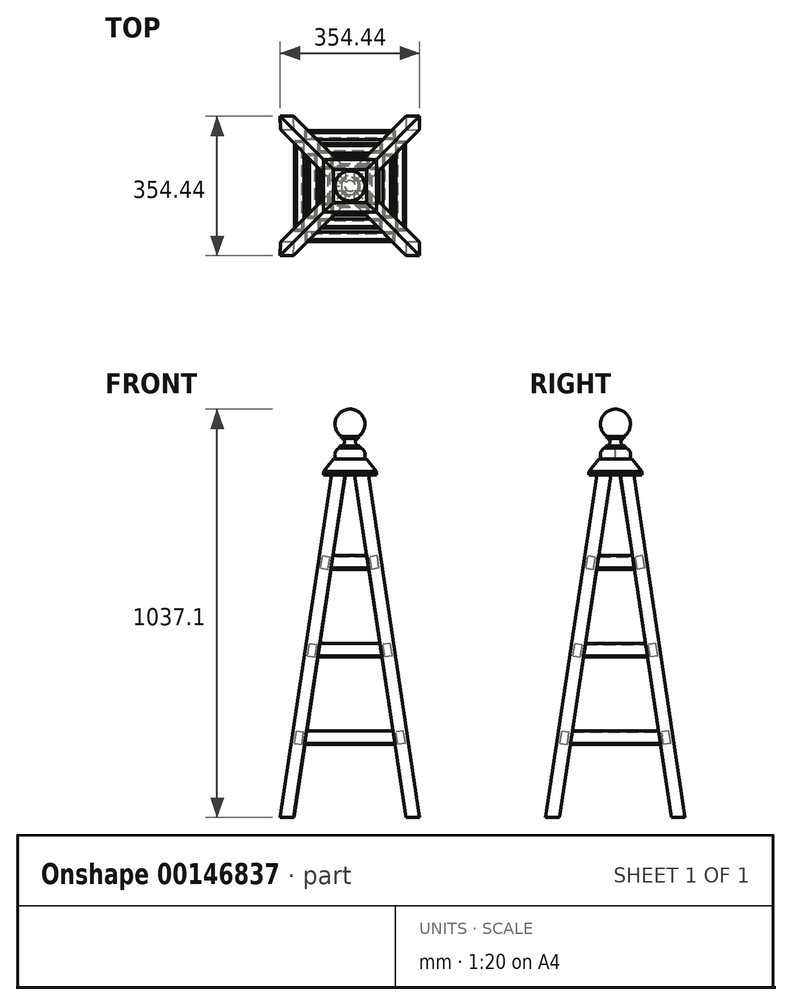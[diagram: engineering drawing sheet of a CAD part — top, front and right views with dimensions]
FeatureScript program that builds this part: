
annotation { "Feature Type Name" : "Feature", "Feature Type Description" : "" }
export const myFeature = defineFeature(function(context is Context, id is Id, definition is map)
    precondition{}
    {
        {
            assignVariable(context, id + "F0", {"name" : "Angle0", "anyValue" : 12 * degree});
        }
        {
            assignVariable(context, id + "F1", {"name" : "CentreSpread0", "anyValue" : 12});
        }
        {
            assignVariable(context, id + "F2", {"name" : "ArmOffset0", "anyValue" : ((((900 - (sqrt(34 * 34 * 2) * sin(getVariable(context, 'Angle0')))) * sin(getVariable(context, 'Angle0')) + (sqrt(17 * 17 * 2) / cos(getVariable(context, 'Angle0')))) * sin(45 * degree)) + getVariable(context, 'CentreSpread0')) * mm});
        }
        {
            var Q0;
            Q0=qCreatedBy(makeId("Front.planeOp"),FACE);
            var sketch = newSketch(context, id + "F3", { "sketchPlane" : qUnion([Q0])});
            skLineSegment(sketch, "E0.bottom", {"start": v(-17, 450) * mm, "end": v(17, 450) * mm});
            skLineSegment(sketch, "E0.top", {"start": v(-17, -450) * mm, "end": v(17, -450) * mm});
            skLineSegment(sketch, "E0.left", {"start": v(-17, 450) * mm, "end": v(-17, -450) * mm});
            skLineSegment(sketch, "E0.right", {"start": v(17, 450) * mm, "end": v(17, -450) * mm});
            skPoint(sketch, "E0.middle", {"position": v(0, 0) * mm});
            skLineSegment(sketch, "E1", {"start": v(0, 0) * mm, "end": v(0, 406.37) * mm, "construction": true});
            skSolve(sketch);
        }
        {
            var Q0;
            Q0=sQuery(id+"F3.wireOp",EDGE,"E1");
            cPlane(context, id + "F4", {"entities" : qUnion([Q0]), "cplaneType" : CPlaneType.LINE_ANGLE, "offset" : 25 * mm, "angle" : 45 * degree, "width" : 150 * mm, "height" : 150 * mm});
        }
        {
            var Q0;
            Q0=sQuery(id+"F3.wireOp",EDGE,"E1");
            cPlane(context, id + "F5", {"entities" : qUnion([Q0]), "cplaneType" : CPlaneType.LINE_ANGLE, "offset" : 25 * mm, "angle" : 135 * degree, "width" : 150 * mm, "height" : 150 * mm});
        }
        {
            var Q0;
            Q0=qCreatedBy(id+"F5.planeOp",FACE);
            cPlane(context, id + "F6", {"entities" : qUnion([Q0]), "cplaneType" : CPlaneType.OFFSET, "offset" : (sqrt(17 * 17 * 2)) * mm, "oppositeDirection" : true, "width" : 150 * mm, "height" : 150 * mm});
        }
        {
            var Q0;
            Q0=qSketchRegion(id+"F3",true);
            extrude(context, id + "F7", {"entities" : qUnion([Q0]), "depth" : 17 * mm, "hasSecondDirection" : true, "secondDirectionOppositeDirection" : true, "secondDirectionDepth" : 17 * mm});
        }
        {
            var Q0;
            Q0=qCreatedBy(id+"F4.planeOp",FACE);
            var sketch = newSketch(context, id + "F8", { "sketchPlane" : qUnion([Q0])});
            skLineSegment(sketch, "E2", {"start": v(24.04, 450) * mm, "end": v(-24.04, 439.78) * mm});
            skLineSegment(sketch, "E3", {"start": v(-24.04, 450) * mm, "end": v(24.04, 450) * mm});
            skLineSegment(sketch, "E4", {"start": v(-24.04, 450) * mm, "end": v(-24.04, 439.78) * mm});
            skLineSegment(sketch, "E5", {"start": v(-24.04, -450) * mm, "end": v(24.04, -439.78) * mm});
            skLineSegment(sketch, "E6", {"start": v(-24.04, -450) * mm, "end": v(24.04, -450) * mm});
            skLineSegment(sketch, "E7", {"start": v(24.04, -450) * mm, "end": v(24.04, -439.78) * mm});
            skSolve(sketch);
        }
        {
            var Q0;
            Q0=qSketchRegion(id+"F8",true);
            extrude(context, id + "F9", {"entities" : qUnion([Q0]), "operationType" : NewBodyOperationType.REMOVE, "depth" : (sqrt(17 * 17 * 2)) * mm, "hasSecondDirection" : true, "secondDirectionOppositeDirection" : true, "secondDirectionDepth" : (sqrt(17 * 17 * 2)) * mm});
        }
        {
            var Q0;
            Q0=qCreatedBy(id+"F6.planeOp",FACE);
            var sketch = newSketch(context, id + "F10", { "sketchPlane" : qUnion([Q0])});
            skLineSegment(sketch, "E8", {"start": v(-24.04, -450) * mm, "end": v(24.04, -450) * mm, "construction": true});
            skSolve(sketch);
        }
        {
            var Q0;
            Q0=makeQuery(id+"F7.opExtrude","SWEPT_BODY",BODY,{"disambiguationData":[OSD([sQuery(id+"F3.wireOp",EDGE,"E0.bottom"),sQuery(id+"F3.wireOp",EDGE,"E0.top"),sQuery(id+"F3.wireOp",EDGE,"E0.left"),sQuery(id+"F3.wireOp",EDGE,"E0.right")])]});
            var Q1;
            Q1=sQuery(id+"F10.wireOp",EDGE,"E8");
            transform(context, id + "F11", {"entities" : qUnion([Q0]), "transformType" : TransformType.ROTATION, "transformAxis" : qUnion([Q1]), "angle" : getVariable(context, 'Angle0'), "makeCopy" : false});
        }
        {
            var Q0;
            Q0=makeQuery(id+"F7.opExtrude","SWEPT_BODY",BODY,{"disambiguationData":[OSD([sQuery(id+"F3.wireOp",EDGE,"E0.bottom"),sQuery(id+"F3.wireOp",EDGE,"E0.top"),sQuery(id+"F3.wireOp",EDGE,"E0.left"),sQuery(id+"F3.wireOp",EDGE,"E0.right")])]});
            transform(context, id + "F12", {"entities" : qUnion([Q0]), "transformType" : TransformType.TRANSLATION_3D, "dx" : getVariable(context, 'ArmOffset0'), "dy" : -getVariable(context, 'ArmOffset0'), "dz" : 0 * mm, "makeCopy" : false});
        }
        {
            var Q0;
            Q0=makeQuery(id+"F7.opExtrude","SWEPT_BODY",BODY,{"disambiguationData":[OSD([sQuery(id+"F3.wireOp",EDGE,"E0.bottom"),sQuery(id+"F3.wireOp",EDGE,"E0.top"),sQuery(id+"F3.wireOp",EDGE,"E0.left"),sQuery(id+"F3.wireOp",EDGE,"E0.right")])]});
            var Q1;
            Q1=sQuery(id+"F3.wireOp",EDGE,"E1");
            circularPattern(context, id + "F13", {"entities" : qUnion([Q0]), "axis" : qUnion([Q1]), "angle" : 360 * degree, "instanceCount" : 4, "equalSpace" : true});
        }
        {
            var Q0;
            Q0=qCreatedBy(makeId("Top.planeOp"),FACE);
            var sketch = newSketch(context, id + "F14", { "sketchPlane" : qUnion([Q0])});
            skLineSegment(sketch, "E9.bottom", {"start": v(67, 67) * mm, "end": v(-67, 67) * mm});
            skLineSegment(sketch, "E9.top", {"start": v(67, -67) * mm, "end": v(-67, -67) * mm});
            skLineSegment(sketch, "E9.left", {"start": v(67, 67) * mm, "end": v(67, -67) * mm});
            skLineSegment(sketch, "E9.right", {"start": v(-67, 67) * mm, "end": v(-67, -67) * mm});
            skPoint(sketch, "E9.middle", {"position": v(0, 0) * mm});
            skSolve(sketch);
        }
        {
            var Q0;
            Q0=qSketchRegion(id+"F14",true);
            extrude(context, id + "F15", {"entities" : qUnion([Q0]), "depth" : 32 * mm, "hasDraft" : true, "draftAngle" : 38 * degree, "draftPullDirection" : true, "hasSecondDirection" : true, "secondDirectionOppositeDirection" : true, "secondDirectionDepth" : 8 * mm});
        }
        {
            var Q0;
            Q0=makeQuery(id+"F15.split0.splitOp","SPLIT",BODY,{"derivedFrom":makeQuery(id+"F15.opExtrude","SWEPT_BODY",BODY,{"disambiguationData":[OSD([sQuery(id+"F14.wireOp",EDGE,"E9.bottom"),sQuery(id+"F14.wireOp",EDGE,"E9.top"),sQuery(id+"F14.wireOp",EDGE,"E9.left"),sQuery(id+"F14.wireOp",EDGE,"E9.right")])]})});
            transform(context, id + "F16", {"entities" : qUnion([Q0]), "transformType" : TransformType.TRANSLATION_3D, "dx" : 0 * mm, "dy" : 0 * mm, "dz" : ((900 * cos(getVariable(context, 'Angle0')) - (tan(getVariable(context, 'Angle0')) * sqrt(34 * 34 * 2)) - 442)) * mm, "makeCopy" : false});
        }
        {
            var Q0;
            Q0=qCreatedBy(makeId("Front.planeOp"),FACE);
            var sketch = newSketch(context, id + "F17", { "sketchPlane" : qUnion([Q0])});
            skLineSegment(sketch, "E10", {"start": v(0, 0) * mm, "end": v(33, 0) * mm});
            skFitSpline(sketch, "E11", {"points": [v(33, 0) * mm, v(38, 16.22) * mm, v(26, 28) * mm], "startDerivative": vector(25.56, 0) * mm, "endDerivative": vector(-18.97, 0) * mm});
            skLineSegment(sketch, "E12", {"start": v(26, 28) * mm, "end": v(26, 33) * mm});
            skFitSpline(sketch, "E13", {"points": [v(26, 33) * mm, v(13.8, 42.6) * mm, v(22, 53) * mm], "startDerivative": vector(-39.34, 1.43) * mm, "endDerivative": vector(35.56, 0.88) * mm});
            skLineSegment(sketch, "E14", {"start": v(22, 53) * mm, "end": v(22, 58) * mm});
            skArc(sketch, "E15", {"start": v(22, 58) * mm, "mid": v(36.2, 100.53) * mm, "end": v(0, 126.98) * mm});
            skLineSegment(sketch, "E16", {"start": v(0, 0) * mm, "end": v(0, 126.98) * mm});
            skSolve(sketch);
        }
        {
            var Q0;
            Q0=makeQuery(id+"F17.imprint","IMPRINT",FACE,{"disambiguationData":[TD([[makeQuery(id+"F17.imprint","IMPRINT",EDGE,{"derivedFrom":sQuery(id+"F17.wireOp",EDGE,"E10")}),1.0]])]});
            var Q1;
            Q1=sQuery(id+"F17.wireOp",EDGE,"E16");
            revolve(context, id + "F18", {"entities" : qUnion([Q0]), "axis" : qUnion([Q1]), "revolveType" : RevolveType.FULL});
        }
        {
            var Q0;
            Q0=makeQuery(id+"F18.opRevolve","SWEPT_BODY",BODY,{"disambiguationData":[OSD([sQuery(id+"F17.wireOp",EDGE,"E10"),sQuery(id+"F17.wireOp",EDGE,"E11"),sQuery(id+"F17.wireOp",EDGE,"E12"),sQuery(id+"F17.wireOp",EDGE,"E13"),sQuery(id+"F17.wireOp",EDGE,"E14"),sQuery(id+"F17.wireOp",EDGE,"E15"),sQuery(id+"F17.wireOp",EDGE,"E16")])]});
            transform(context, id + "F19", {"entities" : qUnion([Q0]), "transformType" : TransformType.TRANSLATION_3D, "dx" : 0 * mm, "dy" : 0 * mm, "dz" : ((900 * cos(getVariable(context, 'Angle0')) - (tan(getVariable(context, 'Angle0')) * sqrt(34 * 34 * 2)) - 410)) * mm, "makeCopy" : false});
        }
        {
            var Q0;
            Q0=qCreatedBy(makeId("Front.planeOp"),FACE);
            var sketch = newSketch(context, id + "F20", { "sketchPlane" : qUnion([Q0])});
            skLineSegment(sketch, "E17", {"start": v(0, -450) * mm, "end": v(0, 420.11) * mm, "construction": true});
            skLineSegment(sketch, "E18", {"start": v(-29.38, 420.11) * mm, "end": v(-29.38, -450) * mm, "construction": true});
            skLineSegment(sketch, "E19.bottom", {"start": v(-74.34, 183.15) * mm, "end": v(-55.54, 180.35) * mm});
            skLineSegment(sketch, "E19.top", {"start": v(-69.61, 214.8) * mm, "end": v(-50.82, 212) * mm});
            skLineSegment(sketch, "E19.left", {"start": v(-74.34, 183.15) * mm, "end": v(-69.61, 214.8) * mm});
            skLineSegment(sketch, "E19.right", {"start": v(-55.54, 180.35) * mm, "end": v(-50.82, 212) * mm});
            skPoint(sketch, "E19.middle", {"position": v(-62.58, 197.58) * mm});
            skLineSegment(sketch, "E20.MirrorCS", {"start": v(55.54, 180.35) * mm, "end": v(50.82, 212) * mm});
            skLineSegment(sketch, "E21.MirrorCS", {"start": v(74.34, 183.15) * mm, "end": v(55.54, 180.35) * mm});
            skLineSegment(sketch, "E22.MirrorCS", {"start": v(74.34, 183.15) * mm, "end": v(69.61, 214.8) * mm});
            skLineSegment(sketch, "E23.MirrorCS", {"start": v(69.61, 214.8) * mm, "end": v(50.82, 212) * mm});
            skLineSegment(sketch, "E24", {"start": v(-29.38, 420.11) * mm, "end": v(-159.2, -450) * mm, "construction": true});
            skLineSegment(sketch, "E25.bottom", {"start": v(-107.54, -39.38) * mm, "end": v(-88.74, -42.19) * mm});
            skLineSegment(sketch, "E25.top", {"start": v(-102.81, -7.74) * mm, "end": v(-84.02, -10.54) * mm});
            skLineSegment(sketch, "E25.left", {"start": v(-107.54, -39.38) * mm, "end": v(-102.81, -7.74) * mm});
            skLineSegment(sketch, "E25.right", {"start": v(-88.74, -42.19) * mm, "end": v(-84.02, -10.54) * mm});
            skPoint(sketch, "E25.middle", {"position": v(-95.78, -24.96) * mm});
            skLineSegment(sketch, "E26.bottom", {"start": v(-140.74, -261.92) * mm, "end": v(-121.94, -264.73) * mm});
            skLineSegment(sketch, "E26.top", {"start": v(-136.01, -230.27) * mm, "end": v(-117.22, -233.08) * mm});
            skLineSegment(sketch, "E26.left", {"start": v(-140.74, -261.92) * mm, "end": v(-136.01, -230.27) * mm});
            skLineSegment(sketch, "E26.right", {"start": v(-121.94, -264.73) * mm, "end": v(-117.22, -233.08) * mm});
            skPoint(sketch, "E26.middle", {"position": v(-128.98, -247.5) * mm});
            skLineSegment(sketch, "E27.MirrorCS", {"start": v(140.74, -261.92) * mm, "end": v(136.01, -230.27) * mm});
            skLineSegment(sketch, "E28.MirrorCS", {"start": v(140.74, -261.92) * mm, "end": v(121.94, -264.73) * mm});
            skLineSegment(sketch, "E29.MirrorCS", {"start": v(121.94, -264.73) * mm, "end": v(117.22, -233.08) * mm});
            skLineSegment(sketch, "E30.MirrorCS", {"start": v(136.01, -230.27) * mm, "end": v(117.22, -233.08) * mm});
            skLineSegment(sketch, "E31.MirrorCS", {"start": v(107.54, -39.38) * mm, "end": v(88.74, -42.19) * mm});
            skLineSegment(sketch, "E32.MirrorCS", {"start": v(107.54, -39.38) * mm, "end": v(102.81, -7.74) * mm});
            skLineSegment(sketch, "E33.MirrorCS", {"start": v(88.74, -42.19) * mm, "end": v(84.02, -10.54) * mm});
            skLineSegment(sketch, "E34.MirrorCS", {"start": v(102.81, -7.74) * mm, "end": v(84.02, -10.54) * mm});
            skSolve(sketch);
        }
        {
            var Q0;
            Q0 = qSketchRegion(id + "F20", true);
            extrude(context, id + "F21", {"entities" : qUnion([Q0]), "endBound" : BoundingType.UP_TO_NEXT, "depth" : 25 * mm, "hasSecondDirection" : true, "secondDirectionBound" : SecondDirectionBoundingType.UP_TO_NEXT, "secondDirectionOppositeDirection" : true, "secondDirectionDepth" : 25 * mm});
        }
        {
            var Q0;
            Q0=makeQuery(id+"F21.opExtrude","SWEPT_BODY",BODY,{"disambiguationData":[OSD([sQuery(id+"F20.wireOp",EDGE,"E19.bottom"),sQuery(id+"F20.wireOp",EDGE,"E19.top"),sQuery(id+"F20.wireOp",EDGE,"E19.left"),sQuery(id+"F20.wireOp",EDGE,"E19.right")])]});
            var Q1;
            Q1=makeQuery(id+"F21.opExtrude","SWEPT_BODY",BODY,{"disambiguationData":[OSD([sQuery(id+"F20.wireOp",EDGE,"E20.MirrorCS"),sQuery(id+"F20.wireOp",EDGE,"E21.MirrorCS"),sQuery(id+"F20.wireOp",EDGE,"E22.MirrorCS"),sQuery(id+"F20.wireOp",EDGE,"E23.MirrorCS")])]});
            var Q2;
            Q2=makeQuery(id+"F21.opExtrude","SWEPT_BODY",BODY,{"disambiguationData":[OSD([sQuery(id+"F20.wireOp",EDGE,"E25.bottom"),sQuery(id+"F20.wireOp",EDGE,"E25.top"),sQuery(id+"F20.wireOp",EDGE,"E25.left"),sQuery(id+"F20.wireOp",EDGE,"E25.right")])]});
            var Q3;
            Q3=makeQuery(id+"F21.opExtrude","SWEPT_BODY",BODY,{"disambiguationData":[OSD([sQuery(id+"F20.wireOp",EDGE,"E26.bottom"),sQuery(id+"F20.wireOp",EDGE,"E26.top"),sQuery(id+"F20.wireOp",EDGE,"E26.left"),sQuery(id+"F20.wireOp",EDGE,"E26.right")])]});
            var Q4;
            Q4=makeQuery(id+"F21.opExtrude","SWEPT_BODY",BODY,{"disambiguationData":[OSD([sQuery(id+"F20.wireOp",EDGE,"E27.MirrorCS"),sQuery(id+"F20.wireOp",EDGE,"E28.MirrorCS"),sQuery(id+"F20.wireOp",EDGE,"E29.MirrorCS"),sQuery(id+"F20.wireOp",EDGE,"E30.MirrorCS")])]});
            var Q5;
            Q5=makeQuery(id+"F21.opExtrude","SWEPT_BODY",BODY,{"disambiguationData":[OSD([sQuery(id+"F20.wireOp",EDGE,"E31.MirrorCS"),sQuery(id+"F20.wireOp",EDGE,"E32.MirrorCS"),sQuery(id+"F20.wireOp",EDGE,"E33.MirrorCS"),sQuery(id+"F20.wireOp",EDGE,"E34.MirrorCS")])]});
            var Q6;
            Q6=sQuery(id+"F20.wireOp",EDGE,"E17");
            transform(context, id + "F22", {"entities" : qUnion([Q0, Q1, Q2, Q3, Q4, Q5]), "transformType" : TransformType.ROTATION, "transformAxis" : qUnion([Q6]), "angle" : 90 * degree, "makeCopy" : true});
        }
    });
